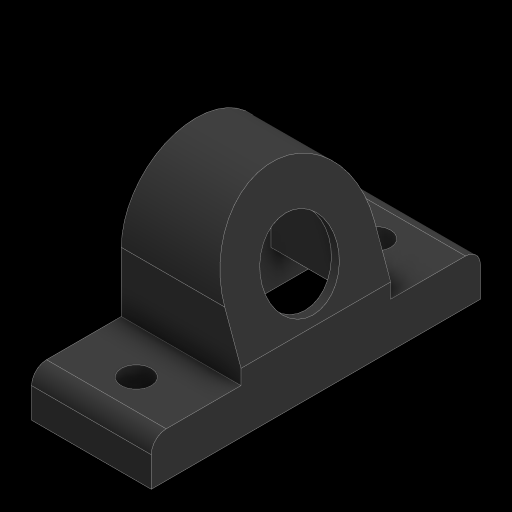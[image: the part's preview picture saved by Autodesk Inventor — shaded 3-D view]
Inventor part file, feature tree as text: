
AUTODESK INVENTOR PART (.ipt)
format: ipt  version: 2024 (Build 280153000, 153)  size: 197,120 bytes
history: native  units: in
note: dims shown in document units (in); Inventor stores cm internally (conversion verified against a paired STEP export)
features: sketch x5, extrude x4, hole x1, mirror x1, fillet x1, shell x1
ambient origin geometry x8: Origin, YZ Plane, XZ Plane, XY Plane, X Axis, Y Axis, Z Axis, Center Point
bodies: Solid1 (feature_tree)
feature tree (13):
  extrude  "BASE"  Depth=4.0in
  extrude  "ARCH"  Depth=5.0in
  extrude  "ANGLED CUT"  TaperAngle=0.0deg  [1 undecoded]
  hole  "Hole1"  [1 undecoded]
  mirror  "Mirror1"
  fillet  "Fillet1"  Radius=0.1374in
  shell  "Shell1"  Thickness=0.0in
  extrude  "Extrusion4"  Depth=4.0in
  sketch  "Sketch1"  dims[d0=11.0in d1=4.0in]
  sketch  "Sketch2"  dims[d2=1.5in d3=0.0in d4=5.0in]
  sketch  "Sketch3"  dims[d5=3.5in d7=0.0in]
  sketch  "Sketch4"  dims[d8=4.0in d9=0.0in d11=2.0in d12=0.1374in d13=0.0in d14=0.0in]
  sketch  "Sketch5"  dims[d15=1.0in d16=0.75in d17=0.375in d18=0.25in d19=0.5635in d20=1.0in d21=0.8108in d22=4.0in d23=2.0in d24=0.5in d25=0.25in d26=2.5in d27=3.5in d28=0.0in d29=1.0in d30=0.0in d31=0.5in d32=0.0344in]
note: 2 required parameter values undecoded (feature->parameter linkage not recoverable at this tier; creation-order binding heuristic only, values carry confidence <= 0.55)
